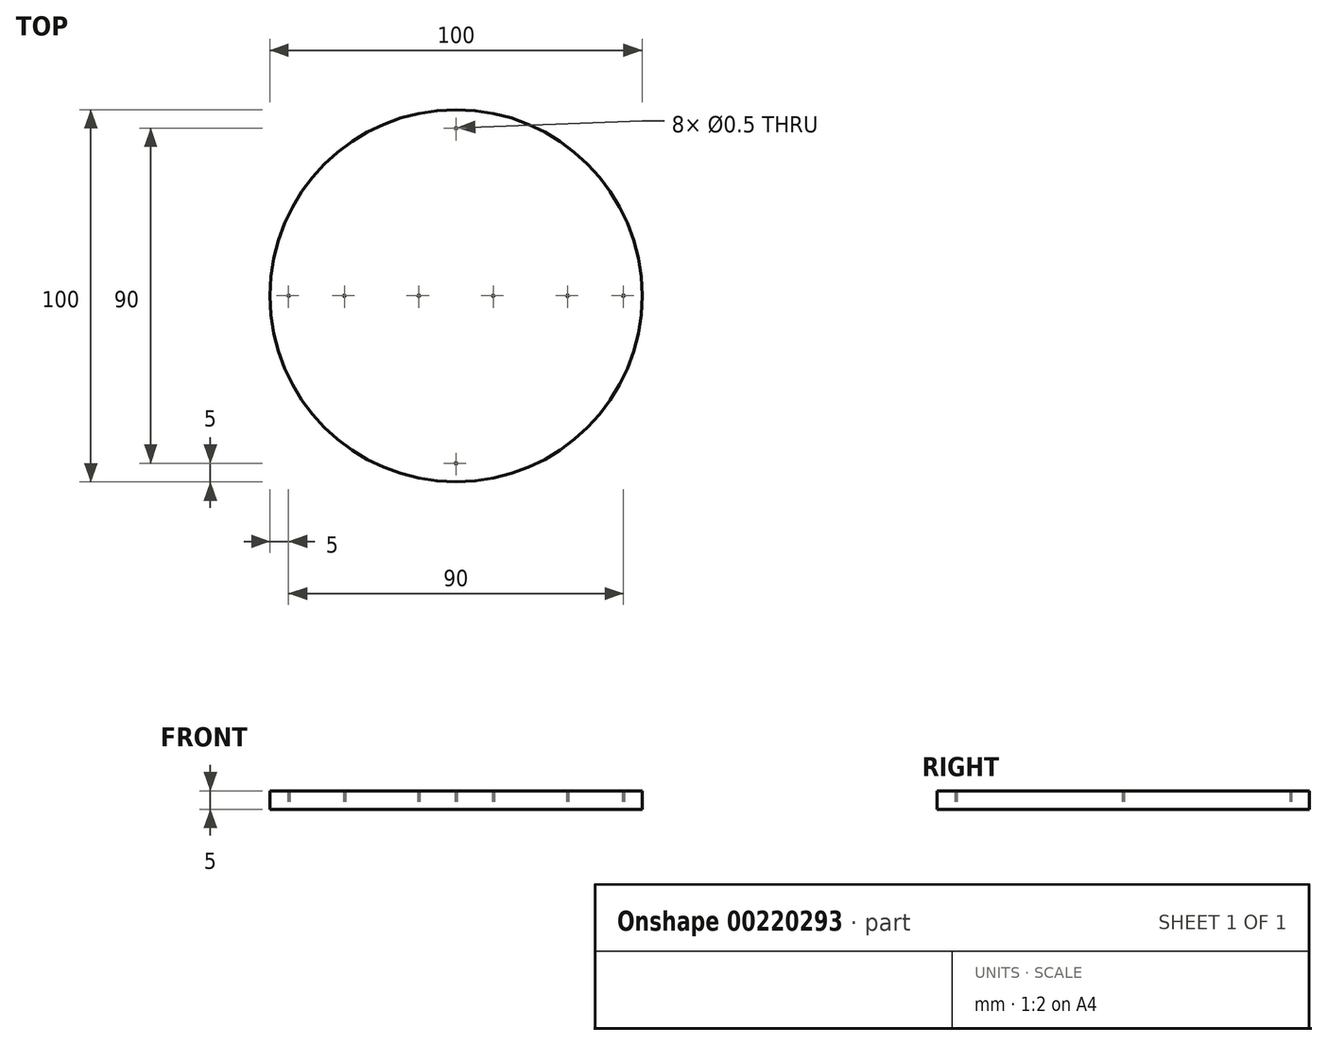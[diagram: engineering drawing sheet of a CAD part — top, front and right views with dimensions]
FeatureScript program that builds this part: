
annotation { "Feature Type Name" : "Feature", "Feature Type Description" : "" }
export const myFeature = defineFeature(function(context is Context, id is Id, definition is map)
    precondition{}
    {
        {
            var Q0;
            Q0=qCreatedBy(makeId("Top.planeOp"),FACE);
            var sketch = newSketch(context, id + "F0", { "sketchPlane" : qUnion([Q0])});
            skCircle(sketch, "E0", {"center": v(0, 0) * mm, "radius": 50 * mm});
            skCircle(sketch, "E1", {"center": v(-45, 0) * mm, "radius": 0.25 * mm});
            skCircle(sketch, "E2", {"center": v(-30, 0) * mm, "radius": 0.25 * mm});
            skCircle(sketch, "E3", {"center": v(-10, 0) * mm, "radius": 0.25 * mm});
            skCircle(sketch, "E4", {"center": v(0, 45) * mm, "radius": 0.25 * mm});
            skLineSegment(sketch, "E5", {"start": v(0, 0) * mm, "end": v(35.36, 35.36) * mm, "construction": true});
            skCircle(sketch, "E6.MirrorC", {"center": v(45, 0) * mm, "radius": 0.25 * mm});
            skCircle(sketch, "E7.MirrorC", {"center": v(30, 0) * mm, "radius": 0.25 * mm});
            skCircle(sketch, "E8.MirrorC", {"center": v(10, 0) * mm, "radius": 0.25 * mm});
            skCircle(sketch, "E9.MirrorC", {"center": v(0, -45) * mm, "radius": 0.25 * mm});
            skSolve(sketch);
        }
        {
            var Q0;
            Q0=makeQuery(id+"F0.imprint","IMPRINT",FACE,{"disambiguationData":[TD([[makeQuery(id+"F0.imprint","IMPRINT",EDGE,{"derivedFrom":sQuery(id+"F0.wireOp",EDGE,"E0")}),1.0]])]});
            extrude(context, id + "F1", {"entities" : qUnion([Q0]), "depth" : 5 * mm});
        }
    });
